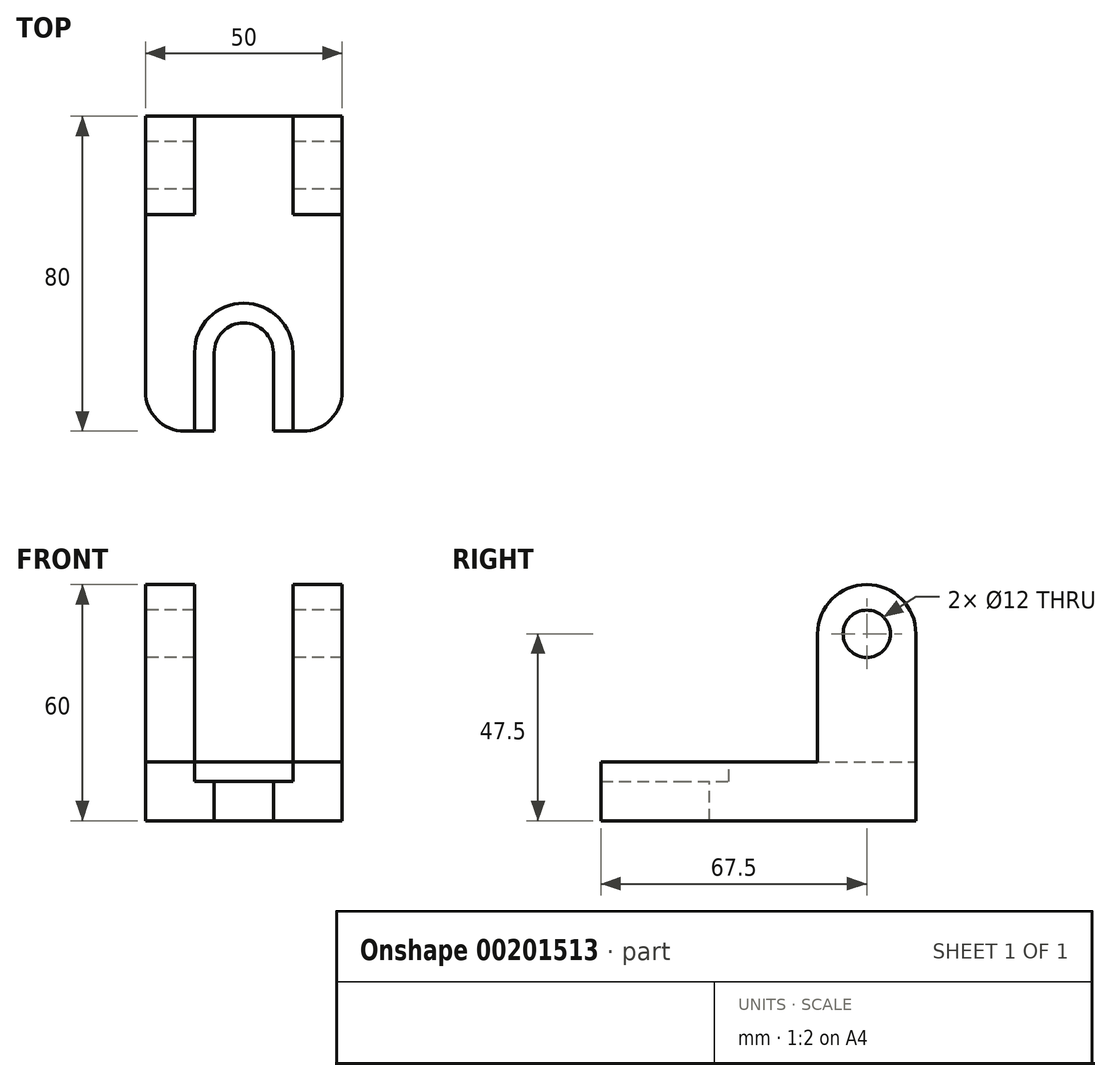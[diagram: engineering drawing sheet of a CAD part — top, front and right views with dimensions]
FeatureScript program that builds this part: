
annotation { "Feature Type Name" : "Feature", "Feature Type Description" : "" }
export const myFeature = defineFeature(function(context is Context, id is Id, definition is map)
    precondition{}
    {
        {
            var Q0;
            Q0=qCreatedBy(makeId("Right.planeOp"),FACE);
            var sketch = newSketch(context, id + "F0", { "sketchPlane" : qUnion([Q0])});
            skLineSegment(sketch, "E0", {"start": v(0, 0) * mm, "end": v(-80, 0) * mm});
            skLineSegment(sketch, "E1", {"start": v(-80, 15) * mm, "end": v(-25, 15) * mm});
            skLineSegment(sketch, "E2", {"start": v(-25, 15) * mm, "end": v(-25, 47.5) * mm});
            skLineSegment(sketch, "E3", {"start": v(-25, 47.5) * mm, "end": v(0, 47.5) * mm});
            skLineSegment(sketch, "E4", {"start": v(0, 47.5) * mm, "end": v(0, 0) * mm});
            skLineSegment(sketch, "E5", {"start": v(-80, 0) * mm, "end": v(-80, 15) * mm});
            skCircle(sketch, "E6", {"center": v(-12.5, 47.5) * mm, "radius": 12.5 * mm});
            skCircle(sketch, "E7", {"center": v(-12.5, 47.5) * mm, "radius": 6 * mm});
            skLineSegment(sketch, "E8", {"start": v(-25, 15) * mm, "end": v(0, 15) * mm});
            skSolve(sketch);
        }
        {
            var Q0;
            Q0=qSketchRegion(id+"F0",true);
            extrude(context, id + "F1", {"entities" : qUnion([Q0]), "endBound" : BoundingType.SYMMETRIC, "depth" : 50 * mm});
        }
        {
            var Q0;
            {var subQ0=sQuery(id+"F0.wireOp",EDGE,"E2");Q0=makeQuery(id+"F0.imprint","IMPRINT",FACE,{"disambiguationData":[TD([[makeQuery(id+"F0.imprint","IMPRINT",EDGE,{"derivedFrom":subQ0}),-1.0]])]});}
            var Q1;
            {var subQ1=sQuery(id+"F0.wireOp",EDGE,"E3");var subQ3=sQuery(id+"F0.wireOp",EDGE,"E7");var subQ4=makeQuery(id+"F0.imprint","INTERSECT",VERTEX,{"disambiguationData":[OD(0.0)],"derivedFrom":[subQ1,subQ3]});Q1=makeQuery(id+"F0.imprint","IMPRINT",FACE,{"disambiguationData":[TD([[makeQuery(id+"F0.imprint","IMPRINT",EDGE,{"disambiguationData":[TD([[subQ4,-1.0]])],"derivedFrom":subQ3}),-1.0]])]});}
            var Q2;
            {var subQ0=sQuery(id+"F0.wireOp",EDGE,"E7");var subQ1=sQuery(id+"F0.wireOp",EDGE,"E3");var subQ2=makeQuery(id+"F0.imprint","INTERSECT",VERTEX,{"disambiguationData":[OD(0.0)],"derivedFrom":[subQ1,subQ0]});Q2=makeQuery(id+"F0.imprint","IMPRINT",FACE,{"disambiguationData":[TD([[makeQuery(id+"F0.imprint","IMPRINT",EDGE,{"disambiguationData":[TD([[subQ2,-1.0]])],"derivedFrom":subQ1}),-1.0]])]});}
            var Q3;
            {var subQ0=sQuery(id+"F0.wireOp",EDGE,"E7");var subQ1=sQuery(id+"F0.wireOp",EDGE,"E3");var subQ2=makeQuery(id+"F0.imprint","INTERSECT",VERTEX,{"disambiguationData":[OD(0.0)],"derivedFrom":[subQ1,subQ0]});Q3=makeQuery(id+"F0.imprint","IMPRINT",FACE,{"disambiguationData":[TD([[makeQuery(id+"F0.imprint","IMPRINT",EDGE,{"disambiguationData":[TD([[subQ2,-1.0]])],"derivedFrom":subQ1}),1.0]])]});}
            var Q4;
            {var subQ1=sQuery(id+"F0.wireOp",EDGE,"E3");var subQ3=sQuery(id+"F0.wireOp",EDGE,"E7");var subQ4=makeQuery(id+"F0.imprint","INTERSECT",VERTEX,{"disambiguationData":[OD(0.0)],"derivedFrom":[subQ1,subQ3]});Q4=makeQuery(id+"F0.imprint","IMPRINT",FACE,{"disambiguationData":[TD([[makeQuery(id+"F0.imprint","IMPRINT",EDGE,{"disambiguationData":[TD([[subQ4,1.0]])],"derivedFrom":subQ3}),-1.0]])]});}
            extrude(context, id + "F2", {"entities" : qUnion([Q0, Q1, Q2, Q3, Q4]), "operationType" : NewBodyOperationType.REMOVE, "endBound" : BoundingType.SYMMETRIC, "oppositeDirection" : true, "depth" : 25 * mm});
        }
        {
            var Q0;
            Q0=makeQuery(id+"F1.opExtrude","CAP_EDGE",EDGE,{"disambiguationData":[OSD([sQuery(id+"F0.wireOp",EDGE,"E5")])],"isStart":false});
            var Q1;
            Q1=makeQuery(id+"F1.opExtrude","CAP_EDGE",EDGE,{"disambiguationData":[OSD([sQuery(id+"F0.wireOp",EDGE,"E5")])],"isStart":true});
            fillet(context, id + "F3", {"entities" : qUnion([Q0, Q1]), "radius" : 10 * mm, "tangentPropagation" : true, "allowEdgeOverflow" : false});
        }
        {
            var Q0;
            Q0=makeQuery(id+"F2.boolean.opBoolean","MERGE",FACE,{"derivedFrom":[makeQuery(id+"F1.opExtrude","SWEPT_FACE",FACE,{"disambiguationData":[OSD([sQuery(id+"F0.wireOp",EDGE,"E1")])]}),makeQuery(id+"F2.opExtrude","SWEPT_FACE",FACE,{"disambiguationData":[OSD([sQuery(id+"F0.wireOp",EDGE,"E8")])]})]});
            var sketch = newSketch(context, id + "F4", { "sketchPlane" : qUnion([Q0])});
            skLineSegment(sketch, "E9", {"start": v(-7.5, -80) * mm, "end": v(-7.5, -60) * mm});
            skLineSegment(sketch, "E10", {"start": v(7.5, -60) * mm, "end": v(7.5, -80) * mm});
            skLineSegment(sketch, "E11", {"start": v(0, -86.6) * mm, "end": v(0, -51.92) * mm, "construction": true});
            skPoint(sketch, "E11.startSnap0", {"position": v(0, -80) * mm});
            skArc(sketch, "E12", {"start": v(7.5, -60) * mm, "mid": v(0, -52.5) * mm, "end": v(-7.5, -60) * mm});
            skLineSegment(sketch, "E13.0", {"start": v(12.5, -60) * mm, "end": v(12.5, -80) * mm});
            skArc(sketch, "E13.1", {"start": v(12.5, -60) * mm, "mid": v(0, -47.5) * mm, "end": v(-12.5, -60) * mm});
            skLineSegment(sketch, "E13.2", {"start": v(-12.5, -80) * mm, "end": v(-12.5, -60) * mm});
            skLineSegment(sketch, "E14.0", {"start": v(-7.5, -30) * mm, "end": v(-20, -30) * mm});
            skLineSegment(sketch, "E14.1", {"start": v(-7.5, -5) * mm, "end": v(-7.5, -30) * mm});
            skLineSegment(sketch, "E14.2", {"start": v(-20, -30) * mm, "end": v(-20, -75) * mm});
            skLineSegment(sketch, "E14.3", {"start": v(7.5, -5) * mm, "end": v(-7.5, -5) * mm});
            skLineSegment(sketch, "E14.4", {"start": v(-20, -75) * mm, "end": v(20, -75) * mm});
            skLineSegment(sketch, "E14.5", {"start": v(20, -75) * mm, "end": v(20, -30) * mm});
            skLineSegment(sketch, "E14.6", {"start": v(20, -30) * mm, "end": v(7.5, -30) * mm});
            skLineSegment(sketch, "E14.7", {"start": v(7.5, -30) * mm, "end": v(7.5, -5) * mm});
            skSolve(sketch);
        }
        {
            var Q0;
            {var subQ0=sQuery(id+"F4.wireOp",EDGE,"E12");Q0=makeQuery(id+"F4.imprint","IMPRINT",FACE,{"disambiguationData":[TD([[makeQuery(id+"F4.imprint","IMPRINT",EDGE,{"derivedFrom":subQ0}),1.0]])]});}
            var Q1;
            {var subQ0=sQuery(id+"F4.wireOp",EDGE,"E9");var subQ3=sQuery(id+"F4.wireOp",EDGE,"E14.4");var subQ4=makeQuery(id+"F4.imprint","INTERSECT",VERTEX,{"derivedFrom":[subQ0,subQ3]});Q1=makeQuery(id+"F4.imprint","IMPRINT",FACE,{"disambiguationData":[TD([[makeQuery(id+"F4.imprint","IMPRINT",EDGE,{"disambiguationData":[TD([[subQ4,-1.0]])],"derivedFrom":subQ3}),-1.0]])]});}
            extrude(context, id + "F5", {"entities" : qUnion([Q0, Q1]), "operationType" : NewBodyOperationType.REMOVE, "endBound" : BoundingType.UP_TO_NEXT, "oppositeDirection" : true, "depth" : 25 * mm});
        }
        {
            var Q0;
            {var subQ4=sQuery(id+"F4.wireOp",EDGE,"E12");Q0=makeQuery(id+"F4.imprint","IMPRINT",FACE,{"disambiguationData":[TD([[makeQuery(id+"F4.imprint","IMPRINT",EDGE,{"derivedFrom":subQ4}),-1.0]])]});}
            var Q1;
            {var subQ0=sQuery(id+"F4.wireOp",EDGE,"E9");var subQ3=sQuery(id+"F4.wireOp",EDGE,"E14.4");var subQ4=makeQuery(id+"F4.imprint","INTERSECT",VERTEX,{"derivedFrom":[subQ0,subQ3]});Q1=makeQuery(id+"F4.imprint","IMPRINT",FACE,{"disambiguationData":[TD([[makeQuery(id+"F4.imprint","IMPRINT",EDGE,{"disambiguationData":[TD([[subQ4,1.0]])],"derivedFrom":subQ3}),-1.0]])]});}
            var Q2;
            {var subQ0=sQuery(id+"F4.wireOp",EDGE,"E10");var subQ3=sQuery(id+"F4.wireOp",EDGE,"E14.4");var subQ4=makeQuery(id+"F4.imprint","INTERSECT",VERTEX,{"derivedFrom":[subQ0,subQ3]});Q2=makeQuery(id+"F4.imprint","IMPRINT",FACE,{"disambiguationData":[TD([[makeQuery(id+"F4.imprint","IMPRINT",EDGE,{"disambiguationData":[TD([[subQ4,-1.0]])],"derivedFrom":subQ3}),-1.0]])]});}
            extrude(context, id + "F6", {"entities" : qUnion([Q0, Q1, Q2]), "operationType" : NewBodyOperationType.REMOVE, "oppositeDirection" : true, "depth" : 5 * mm});
        }
    });
